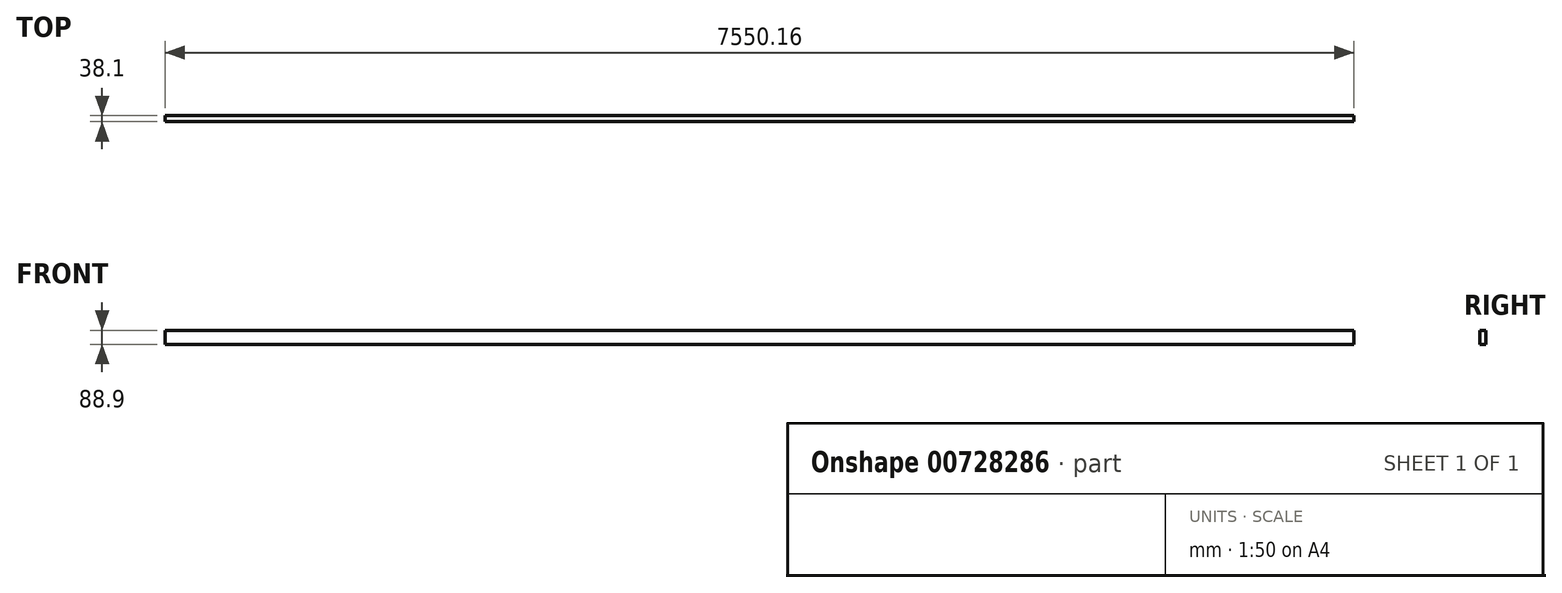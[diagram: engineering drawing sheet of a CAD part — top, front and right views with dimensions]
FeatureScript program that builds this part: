
annotation { "Feature Type Name" : "Feature", "Feature Type Description" : "" }
export const myFeature = defineFeature(function(context is Context, id is Id, definition is map)
    precondition{}
    {
        {
            var Q0;
            Q0=qCreatedBy(makeId("Front.planeOp"),FACE);
            var sketch = newSketch(context, id + "F0", { "sketchPlane" : qUnion([Q0])});
            skLineSegment(sketch, "E0.bottom", {"start": v(-3775.08, -44.45) * mm, "end": v(3775.08, -44.45) * mm});
            skLineSegment(sketch, "E0.top", {"start": v(-3775.08, 44.45) * mm, "end": v(3775.08, 44.45) * mm});
            skLineSegment(sketch, "E0.left", {"start": v(-3775.08, -44.45) * mm, "end": v(-3775.08, 44.45) * mm});
            skLineSegment(sketch, "E0.right", {"start": v(3775.08, -44.45) * mm, "end": v(3775.08, 44.45) * mm});
            skPoint(sketch, "E0.middle", {"position": v(0, 0) * mm});
            skSolve(sketch);
        }
        {
            var Q0;
            Q0=qSketchRegion(id+"F0",true);
            extrude(context, id + "F1", {"entities" : qUnion([Q0]), "depth" : 38.1 * mm, "offsetDistance" : 25.4 * mm});
        }
    });
